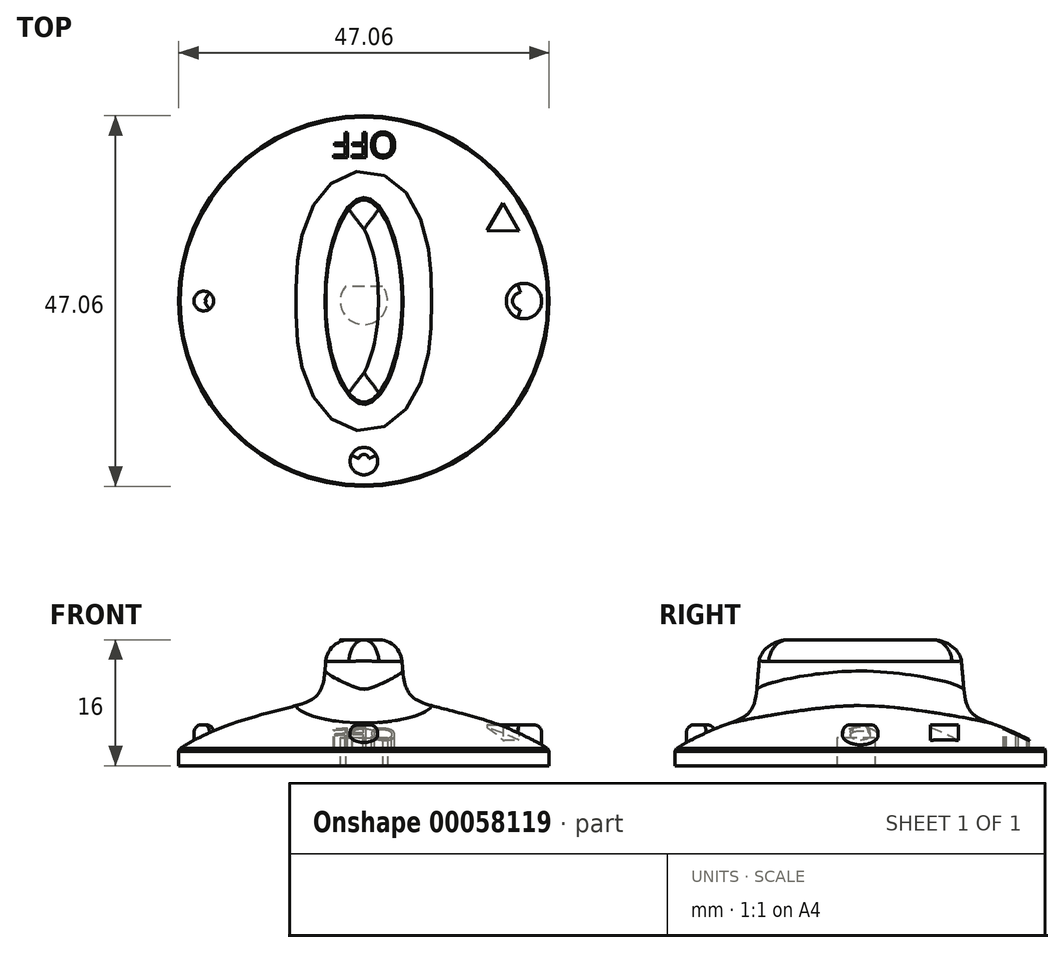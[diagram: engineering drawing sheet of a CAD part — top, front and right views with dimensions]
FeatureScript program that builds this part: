
annotation { "Feature Type Name" : "Feature", "Feature Type Description" : "" }
export const myFeature = defineFeature(function(context is Context, id is Id, definition is map)
    precondition{}
    {
        {
            var Q0;
            Q0=qCreatedBy(makeId("Front.planeOp"),FACE);
            var sketch = newSketch(context, id + "F0", { "sketchPlane" : qUnion([Q0])});
            skLineSegment(sketch, "E0", {"start": v(0, 0) * mm, "end": v(0, 10) * mm});
            skLineSegment(sketch, "E1", {"start": v(0, 0) * mm, "end": v(26, 0) * mm});
            skPoint(sketch, "E2.1.internal.snap0", {"position": v(13, 0) * mm});
            skFitSpline(sketch, "E2", {"points": [v(0, 10) * mm, v(10.49, 7.14) * mm, v(26, 0) * mm], "startDerivative": vector(40.43, -10.8) * mm, "endDerivative": vector(23.77, -23.9) * mm});
            skLineSegment(sketch, "E3", {"start": v(23.53, 0) * mm, "end": v(23.53, 2.05) * mm});
            skSolve(sketch);
        }
        {
            var Q0;
            Q0=makeQuery(id+"F0.imprint","IMPRINT",FACE,{"disambiguationData":[TD([[makeQuery(id+"F0.imprint","IMPRINT",EDGE,{"derivedFrom":sQuery(id+"F0.wireOp",EDGE,"E0")}),-1.0]])]});
            var Q1;
            Q1=sQuery(id+"F0.wireOp",EDGE,"E0");
            revolve(context, id + "F1", {"entities" : qUnion([Q0]), "axis" : qUnion([Q1]), "revolveType" : RevolveType.FULL});
        }
        {
            var Q0;
            Q0=qCreatedBy(makeId("Top.planeOp"),FACE);
            var sketch = newSketch(context, id + "F2", { "sketchPlane" : qUnion([Q0])});
            skEllipse(sketch, "E4", {"center": v(0, 0) * mm, "majorRadius": 14 * mm, "minorRadius": 6 * mm, "majorAxis": v(0, -1)});
            skCircle(sketch, "E5", {"center": v(0, 0) * mm, "radius": 20.26 * mm});
            skSolve(sketch);
        }
        {
            var Q0;
            Q0=makeQuery(id+"F2.imprint","IMPRINT",FACE,{"disambiguationData":[TD([[makeQuery(id+"F2.imprint","IMPRINT",EDGE,{"derivedFrom":sQuery(id+"F2.wireOp",EDGE,"E4")}),1.0]])]});
            extrude(context, id + "F3", {"entities" : qUnion([Q0]), "operationType" : NewBodyOperationType.ADD, "depth" : 16 * mm, "hasDraft" : true, "draftAngle" : 5 * degree, "draftPullDirection" : true});
        }
        {
            var Q0;
            Q0=makeQuery(id+"F3.opExtrude","CAP_EDGE",EDGE,{"disambiguationData":[OSD([sQuery(id+"F2.wireOp",EDGE,"E4")])],"isStart":false});
            fillet(context, id + "F4", {"entities" : qUnion([Q0]), "radius" : 3 * mm, "tangentPropagation" : true, "allowEdgeOverflow" : false});
        }
        {
            var Q0;
            Q0=makeQuery(id+"F3.boolean.opBoolean","INTERSECT",EDGE,{"derivedFrom":[makeQuery(id+"F1.opRevolve","SWEPT_FACE",FACE,{"disambiguationData":[OSD([sQuery(id+"F0.wireOp",EDGE,"E2")])]}),makeQuery(id+"F3.opExtrude","SWEPT_FACE",FACE,{"disambiguationData":[OSD([sQuery(id+"F2.wireOp",EDGE,"E4")])]})]});
            fillet(context, id + "F5", {"entities" : qUnion([Q0]), "radius" : 5 * mm, "tangentPropagation" : true, "rho" : .6, "crossSection" : FilletCrossSection.CONIC, "allowEdgeOverflow" : false});
        }
        {
            var Q0;
            Q0=qCreatedBy(makeId("Top.planeOp"),FACE);
            var sketch = newSketch(context, id + "F6", { "sketchPlane" : qUnion([Q0])});
            skCircle(sketch, "E6", {"center": v(0, 0) * mm, "radius": 5 * mm});
            skArc(sketch, "E7", {"start": v(-2.36, 1.85) * mm, "mid": v(0, -3) * mm, "end": v(2.36, 1.85) * mm});
            skLineSegment(sketch, "E8.rect.bottom", {"start": v(6.97, -7.02) * mm, "end": v(-6.97, -7.02) * mm});
            skLineSegment(sketch, "E8.rect.top", {"start": v(6.97, 7.02) * mm, "end": v(-6.97, 7.02) * mm});
            skLineSegment(sketch, "E8.rect.left", {"start": v(6.97, -7.02) * mm, "end": v(6.97, 7.02) * mm});
            skLineSegment(sketch, "E8.rect.right", {"start": v(-6.97, -7.02) * mm, "end": v(-6.97, 7.02) * mm});
            skLineSegment(sketch, "E9", {"start": v(0, 1.85) * mm, "end": v(-2.36, 1.85) * mm});
            skLineSegment(sketch, "E10", {"start": v(-2.36, 1.85) * mm, "end": v(2.36, 1.85) * mm});
            skPoint(sketch, "E11.orphan", {"position": v(0, -3) * mm});
            skSolve(sketch);
        }
        {
            var Q0;
            {var subQ0=sQuery(id+"F6.wireOp",EDGE,"E7");Q0=makeQuery(id+"F6.imprint","IMPRINT",FACE,{"disambiguationData":[TD([[makeQuery(id+"F6.imprint","IMPRINT",EDGE,{"derivedFrom":subQ0}),1.0]])]});}
            extrude(context, id + "F7", {"entities" : qUnion([Q0]), "operationType" : NewBodyOperationType.REMOVE, "depth" : 3.5 * mm});
        }
        {
            var Q0;
            Q0=qCreatedBy(makeId("Top.planeOp"),FACE);
            var sketch = newSketch(context, id + "F8", { "sketchPlane" : qUnion([Q0])});
            skText(sketch, "E12", { "text": "OFF", "fontName": "OpenSans-Regular.ttf"});
            skLineSegment(sketch, "E13", {"start": v(4.18, 18.21) * mm, "end": v(-3.82, 18.21) * mm, "construction": true});
            const initialGuessF8  = {"E12": [0.00418, 0.02143, -1, 0, 0.00322]};
            skSetInitialGuess(sketch, initialGuessF8);
            skSolve(sketch);
        }
        {
            var Q0;
            Q0 = qSketchRegion(id + "F8", true);
            extrude(context, id + "F9", {"entities" : qUnion([Q0]), "operationType" : NewBodyOperationType.ADD, "depth" : 5.2 * mm});
        }
        {
            var Q0;
            Q0=qCreatedBy(makeId("Top.planeOp"),FACE);
            var sketch = newSketch(context, id + "F10", { "sketchPlane" : qUnion([Q0])});
            skCircle(sketch, "E14", {"center": v(0, 0) * mm, "radius": 20.34 * mm, "construction": true});
            skCircle(sketch, "E15", {"center": v(20.34, 0) * mm, "radius": 2.25 * mm});
            skCircle(sketch, "E16", {"center": v(0, -20.34) * mm, "radius": 1.75 * mm});
            skCircle(sketch, "E17", {"center": v(-20.34, 0) * mm, "radius": 1.25 * mm});
            skLineSegment(sketch, "E18", {"start": v(0, 0) * mm, "end": v(17.65, 10.1) * mm});
            skCircle(sketch, "E19.cCircle", {"center": v(17.65, 10.1) * mm, "radius": 2.35 * mm, "construction": true});
            skLineSegment(sketch, "E19.0", {"start": v(15.61, 8.93) * mm, "end": v(17.66, 12.44) * mm});
            skLineSegment(sketch, "E19.1", {"start": v(17.66, 12.44) * mm, "end": v(19.69, 8.9) * mm});
            skLineSegment(sketch, "E19.2", {"start": v(19.69, 8.9) * mm, "end": v(15.61, 8.93) * mm});
            skSolve(sketch);
        }
        {
            var Q0;
            Q0=makeQuery(id+"F10.imprint","IMPRINT",FACE,{"disambiguationData":[TD([[makeQuery(id+"F10.imprint","IMPRINT",EDGE,{"derivedFrom":sQuery(id+"F10.wireOp",EDGE,"E15")}),1.0]])]});
            var Q1;
            Q1=makeQuery(id+"F10.imprint","IMPRINT",FACE,{"disambiguationData":[TD([[makeQuery(id+"F10.imprint","IMPRINT",EDGE,{"derivedFrom":sQuery(id+"F10.wireOp",EDGE,"E19.0")}),-1.0]])]});
            var Q2;
            Q2=makeQuery(id+"F10.imprint","IMPRINT",FACE,{"disambiguationData":[TD([[makeQuery(id+"F10.imprint","IMPRINT",EDGE,{"derivedFrom":sQuery(id+"F10.wireOp",EDGE,"E16")}),1.0]])]});
            var Q3;
            Q3=makeQuery(id+"F10.imprint","IMPRINT",FACE,{"disambiguationData":[TD([[makeQuery(id+"F10.imprint","IMPRINT",EDGE,{"derivedFrom":sQuery(id+"F10.wireOp",EDGE,"E17")}),1.0]])]});
            extrude(context, id + "F11", {"entities" : qUnion([Q0, Q1, Q2, Q3]), "operationType" : NewBodyOperationType.ADD, "depth" : 5.2 * mm});
        }
        {
            var Q0;
            Q0=makeQuery(id+"F11.opExtrude","CAP_EDGE",EDGE,{"disambiguationData":[OSD([sQuery(id+"F10.wireOp",EDGE,"E15")])],"isStart":false});
            var Q1;
            Q1=makeQuery(id+"F11.opExtrude","CAP_EDGE",EDGE,{"disambiguationData":[OSD([sQuery(id+"F10.wireOp",EDGE,"E16")])],"isStart":false});
            var Q2;
            Q2=makeQuery(id+"F11.opExtrude","CAP_EDGE",EDGE,{"disambiguationData":[OSD([sQuery(id+"F10.wireOp",EDGE,"E17")])],"isStart":false});
            fillet(context, id + "F12", {"entities" : qUnion([Q0, Q1, Q2]), "radius" : 1 * mm, "tangentPropagation" : true, "allowEdgeOverflow" : false});
        }
        {
            var Q0;
            Q0=makeQuery(id+"F9.opExtrude","CAP_FACE",FACE,{"disambiguationData":[OSD([sQuery(id+"F8.wireOp",EDGE,"E12.sketch_text.stroke-16"),sQuery(id+"F8.wireOp",EDGE,"E12.sketch_text.stroke-17"),sQuery(id+"F8.wireOp",EDGE,"E12.sketch_text.stroke-18"),sQuery(id+"F8.wireOp",EDGE,"E12.sketch_text.stroke-19"),sQuery(id+"F8.wireOp",EDGE,"E12.sketch_text.stroke-20"),sQuery(id+"F8.wireOp",EDGE,"E12.sketch_text.stroke-21"),sQuery(id+"F8.wireOp",EDGE,"E12.sketch_text.stroke-22"),sQuery(id+"F8.wireOp",EDGE,"E12.sketch_text.stroke-23"),sQuery(id+"F8.wireOp",EDGE,"E12.sketch_text.stroke-24"),sQuery(id+"F8.wireOp",EDGE,"E12.sketch_text.stroke-25")])],"isStart":false});
            var Q1;
            Q1=makeQuery(id+"F9.opExtrude","CAP_FACE",FACE,{"disambiguationData":[OSD([sQuery(id+"F8.wireOp",EDGE,"E12.sketch_text.stroke-0"),sQuery(id+"F8.wireOp",EDGE,"E12.sketch_text.stroke-1"),sQuery(id+"F8.wireOp",EDGE,"E12.sketch_text.stroke-2"),sQuery(id+"F8.wireOp",EDGE,"E12.sketch_text.stroke-3"),sQuery(id+"F8.wireOp",EDGE,"E12.sketch_text.stroke-4"),sQuery(id+"F8.wireOp",EDGE,"E12.sketch_text.stroke-5"),sQuery(id+"F8.wireOp",EDGE,"E12.sketch_text.stroke-6"),sQuery(id+"F8.wireOp",EDGE,"E12.sketch_text.stroke-7"),sQuery(id+"F8.wireOp",EDGE,"E12.sketch_text.stroke-8"),sQuery(id+"F8.wireOp",EDGE,"E12.sketch_text.stroke-9"),sQuery(id+"F8.wireOp",EDGE,"E12.sketch_text.stroke-10"),sQuery(id+"F8.wireOp",EDGE,"E12.sketch_text.stroke-11"),sQuery(id+"F8.wireOp",EDGE,"E12.sketch_text.stroke-12"),sQuery(id+"F8.wireOp",EDGE,"E12.sketch_text.stroke-13"),sQuery(id+"F8.wireOp",EDGE,"E12.sketch_text.stroke-14"),sQuery(id+"F8.wireOp",EDGE,"E12.sketch_text.stroke-15")])],"isStart":false});
            var Q2;
            Q2=makeQuery(id+"F9.opExtrude","CAP_FACE",FACE,{"disambiguationData":[OSD([sQuery(id+"F8.wireOp",EDGE,"E12.sketch_text.stroke-26"),sQuery(id+"F8.wireOp",EDGE,"E12.sketch_text.stroke-27"),sQuery(id+"F8.wireOp",EDGE,"E12.sketch_text.stroke-28"),sQuery(id+"F8.wireOp",EDGE,"E12.sketch_text.stroke-29"),sQuery(id+"F8.wireOp",EDGE,"E12.sketch_text.stroke-30"),sQuery(id+"F8.wireOp",EDGE,"E12.sketch_text.stroke-31"),sQuery(id+"F8.wireOp",EDGE,"E12.sketch_text.stroke-32"),sQuery(id+"F8.wireOp",EDGE,"E12.sketch_text.stroke-33"),sQuery(id+"F8.wireOp",EDGE,"E12.sketch_text.stroke-34"),sQuery(id+"F8.wireOp",EDGE,"E12.sketch_text.stroke-35")])],"isStart":false});
            extrude(context, id + "F13", {"entities" : qUnion([Q0, Q1, Q2]), "operationType" : NewBodyOperationType.REMOVE, "oppositeDirection" : true, "depth" : 3 * mm});
        }
        {
            var Q0;
            Q0=makeQuery(id+"F1.opRevolve","SWEPT_EDGE",EDGE,{"disambiguationData":[OSD([sQuery(id+"F0.wireOp",EDGE,"E2"),sQuery(id+"F0.wireOp",EDGE,"E3")])]});
            chamfer(context, id + "F14", {"entities" : qUnion([Q0]), "width" : .4 * mm, "tangentPropagation" : true});
        }
    });
